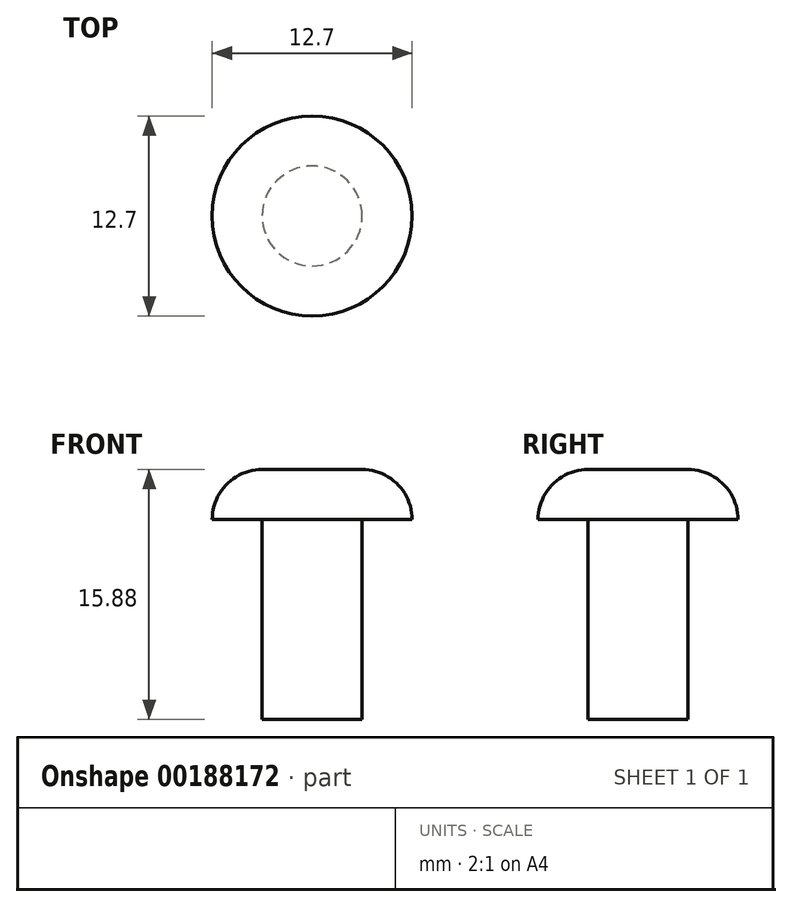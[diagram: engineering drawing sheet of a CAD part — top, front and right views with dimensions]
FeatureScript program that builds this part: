
annotation { "Feature Type Name" : "Feature", "Feature Type Description" : "" }
export const myFeature = defineFeature(function(context is Context, id is Id, definition is map)
    precondition{}
    {
        {
            var Q0;
            Q0=qCreatedBy(makeId("Front.planeOp"),FACE);
            var sketch = newSketch(context, id + "F0", { "sketchPlane" : qUnion([Q0])});
            skLineSegment(sketch, "E0", {"start": v(0, 0) * mm, "end": v(3.18, 0) * mm});
            skLineSegment(sketch, "E1", {"start": v(3.17, 0) * mm, "end": v(3.18, 12.7) * mm});
            skLineSegment(sketch, "E2", {"start": v(3.17, 12.7) * mm, "end": v(6.35, 12.7) * mm});
            skLineSegment(sketch, "E3", {"start": v(0, 0) * mm, "end": v(0, 15.88) * mm});
            skLineSegment(sketch, "E4", {"start": v(0, 15.88) * mm, "end": v(3.17, 15.88) * mm});
            skLineSegment(sketch, "E5", {"start": v(0, 27.15) * mm, "end": v(0, -11.23) * mm, "construction": true});
            skArc(sketch, "E6", {"start": v(6.35, 12.7) * mm, "mid": v(5.42, 14.95) * mm, "end": v(3.17, 15.88) * mm});
            skSolve(sketch);
        }
        {
            var Q0;
            Q0=makeQuery(id+"F0.imprint","IMPRINT",FACE,{"disambiguationData":[TD([[makeQuery(id+"F0.imprint","IMPRINT",EDGE,{"derivedFrom":sQuery(id+"F0.wireOp",EDGE,"E0")}),1.0]])]});
            var Q1;
            Q1=sQuery(id+"F0.wireOp",EDGE,"E5");
            revolve(context, id + "F1", {"entities" : qUnion([Q0]), "axis" : qUnion([Q1]), "revolveType" : RevolveType.FULL});
        }
    });
